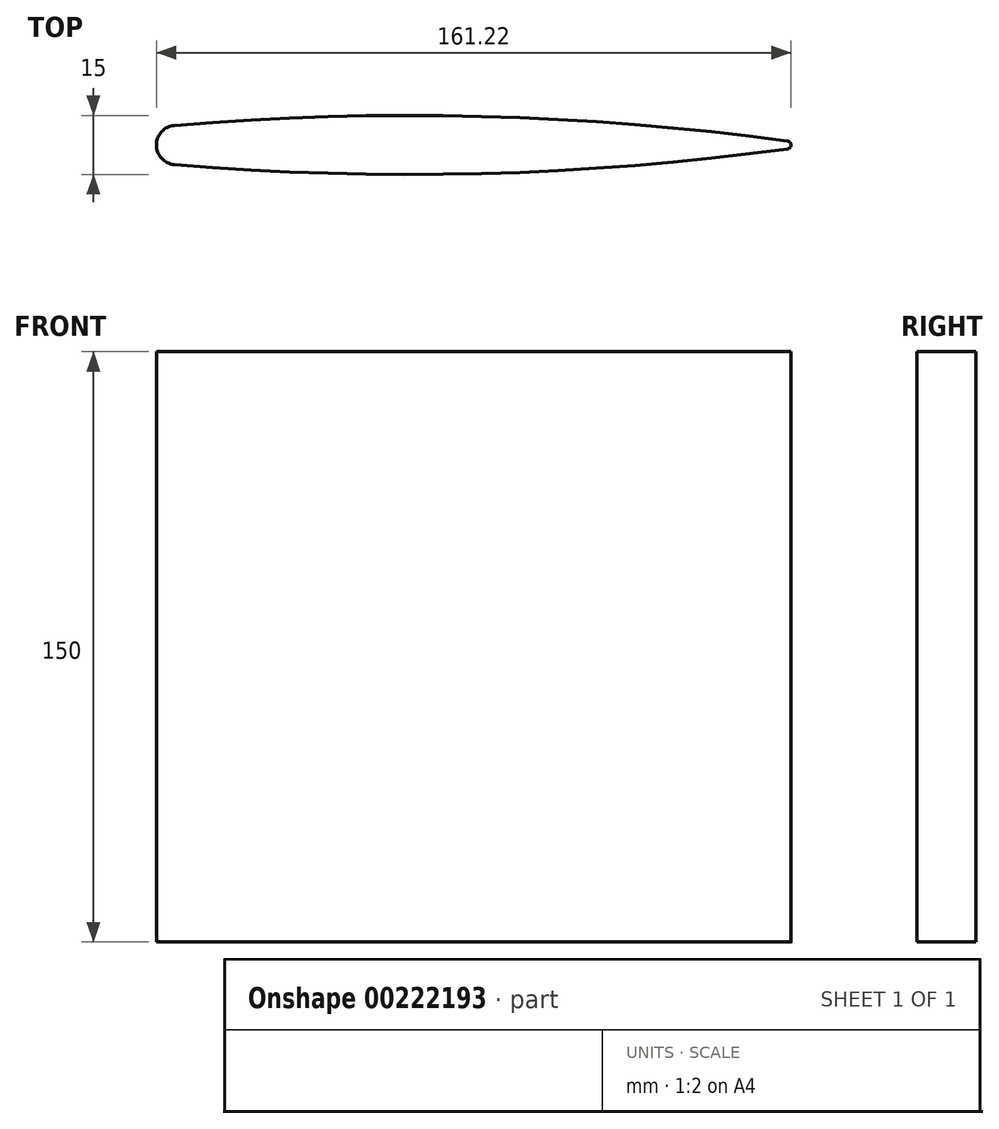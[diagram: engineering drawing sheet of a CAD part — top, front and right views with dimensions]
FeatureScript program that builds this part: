
annotation { "Feature Type Name" : "Feature", "Feature Type Description" : "" }
export const myFeature = defineFeature(function(context is Context, id is Id, definition is map)
    precondition{}
    {
        {
            var Q0;
            Q0=qCreatedBy(makeId("Top.planeOp"),FACE);
            var sketch = newSketch(context, id + "F0", { "sketchPlane" : qUnion([Q0])});
            skLineSegment(sketch, "E0", {"start": v(-79.24, 0) * mm, "end": v(126.76, 0) * mm});
            skArc(sketch, "E1", {"start": v(126.76, 0) * mm, "mid": v(23.76, 7.5) * mm, "end": v(-79.24, 0) * mm});
            skArc(sketch, "E2", {"start": v(-79.24, 0) * mm, "mid": v(23.76, -7.5) * mm, "end": v(126.76, 0) * mm});
            skSolve(sketch);
        }
        {
            var Q0;
            Q0=makeQuery(id+"F0.imprint","IMPRINT",FACE,{"disambiguationData":[TD([[makeQuery(id+"F0.imprint","IMPRINT",EDGE,{"derivedFrom":sQuery(id+"F0.wireOp",EDGE,"E0")}),-1.0]])]});
            var Q1;
            Q1=makeQuery(id+"F0.imprint","IMPRINT",FACE,{"disambiguationData":[TD([[makeQuery(id+"F0.imprint","IMPRINT",EDGE,{"derivedFrom":sQuery(id+"F0.wireOp",EDGE,"E0")}),1.0]])]});
            extrude(context, id + "F1", {"entities" : qUnion([Q0, Q1]), "depth" : 150 * mm});
        }
        {
            var Q0;
            {var subQ0=sQuery(id+"F0.wireOp",EDGE,"E2");var subQ1=sQuery(id+"F0.wireOp",EDGE,"E1");var subQ2=sQuery(id+"F0.wireOp",EDGE,"E0");Q0=makeQuery(id+"F1.opExtrude","SWEPT_EDGE",EDGE,{"disambiguationData":[OSD([subQ2,subQ1,subQ0]),TDD([makeQuery(id+"F0.imprint","INTERSECT",VERTEX,{"disambiguationData":[OD(0.0)],"derivedFrom":[subQ2,subQ1,subQ0]})])]});}
            fillet(context, id + "F2", {"entities" : qUnion([Q0]), "radius" : 5 * mm, "tangentPropagation" : true, "allowEdgeOverflow" : false});
        }
        {
            var Q0;
            {var subQ0=sQuery(id+"F0.wireOp",EDGE,"E2");var subQ1=sQuery(id+"F0.wireOp",EDGE,"E1");var subQ2=sQuery(id+"F0.wireOp",EDGE,"E0");Q0=makeQuery(id+"F1.opExtrude","SWEPT_EDGE",EDGE,{"disambiguationData":[OSD([subQ2,subQ1,subQ0]),TDD([makeQuery(id+"F0.imprint","INTERSECT",VERTEX,{"disambiguationData":[OD(1.0)],"derivedFrom":[subQ2,subQ1,subQ0]})])]});}
            fillet(context, id + "F3", {"entities" : qUnion([Q0]), "radius" : 1 * mm, "tangentPropagation" : true, "allowEdgeOverflow" : false});
        }
    });
